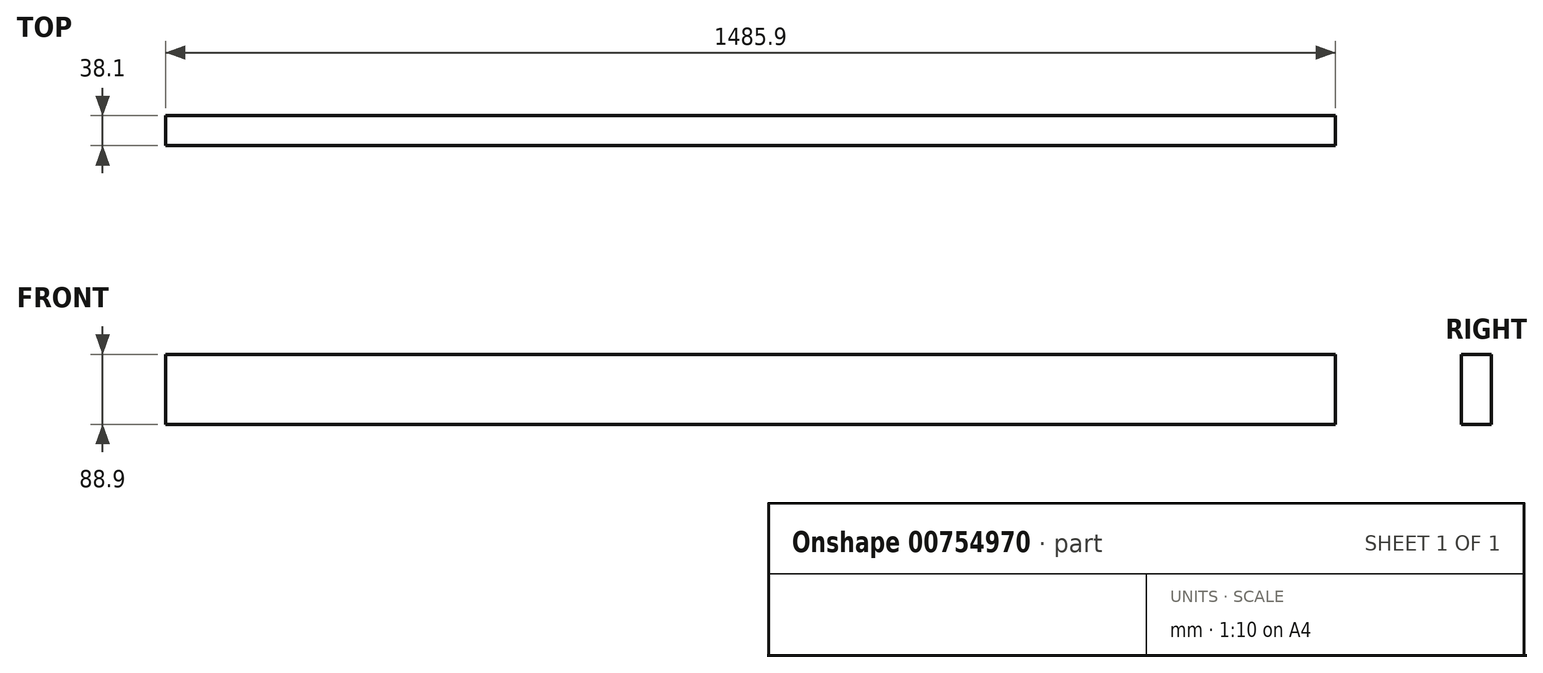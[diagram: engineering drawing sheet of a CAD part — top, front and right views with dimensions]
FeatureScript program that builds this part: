
annotation { "Feature Type Name" : "Feature", "Feature Type Description" : "" }
export const myFeature = defineFeature(function(context is Context, id is Id, definition is map)
    precondition{}
    {
        {
            var Q0;
            Q0=qCreatedBy(makeId("Right.planeOp"),FACE);
            var sketch = newSketch(context, id + "F0", { "sketchPlane" : qUnion([Q0])});
            skLineSegment(sketch, "E0.bottom", {"start": v(0, 0) * mm, "end": v(38.1, 0) * mm});
            skLineSegment(sketch, "E0.top", {"start": v(0, 88.9) * mm, "end": v(38.1, 88.9) * mm});
            skLineSegment(sketch, "E0.left", {"start": v(0, 0) * mm, "end": v(0, 88.9) * mm});
            skLineSegment(sketch, "E0.right", {"start": v(38.1, 0) * mm, "end": v(38.1, 88.9) * mm});
            skSolve(sketch);
        }
        {
            var Q0;
            Q0=makeQuery(id+"F0.imprint","IMPRINT",FACE,{"disambiguationData":[TD([[makeQuery(id+"F0.imprint","IMPRINT",EDGE,{"derivedFrom":sQuery(id+"F0.wireOp",EDGE,"E0.bottom")}),1.0]])]});
            extrude(context, id + "F1", {"entities" : qUnion([Q0]), "depth" : 1485.9 * mm, "offsetDistance" : 25.4 * mm});
        }
    });
